# Revit family: TET1LA
name_source: partatom
category: Generic Models
revit_build: Autodesk Revit LT 2015 (Build: 20140606_1530(x64)
units: mm (PartAtom-declared; Revit-internal decimal feet)

## types (1)
- TET1LA
    Codes/Standards = • Meets or exceeds ASSE 1037, CSA B125.3
• Certifi cations: IAPMO(cUPC), EPA WaterSense,
ASSE, State of Massachusetts, and others
• Code Compliance: UPC, IPC, NSPC, NPC Canada,
and others
• Complies with CA Title 20 regulations and
CalGreen when used with a 1.28 gpf water closet
• ADA compliant
    Colors/Finishes = #CP Polished Chrome
    Manufacturer = TOTO USA
    Model = TET1LA32#CP
    Specifications = • Material Bronze casting
• Power supply EcoPower
• Sensor detection time Factory setting at six
(6) seconds minimum
• Sensor detection range Self-adjusting to
environment
• Discharge quantity Preset to 1.28 gpf/
4.8 lpf
• Operating temperature 32°-104°F (0°-40°C)
• Water supply pressure 35 psi - 125 psi*
• Water supply connection 1" NPT
• Warranty Three year limited
    h = 0' - 11 1/8"
    material = Steel, Galvanized

## geometry (parser evidence)
native form markers: Sweep x2
no freeform markers — native parametric forms only
